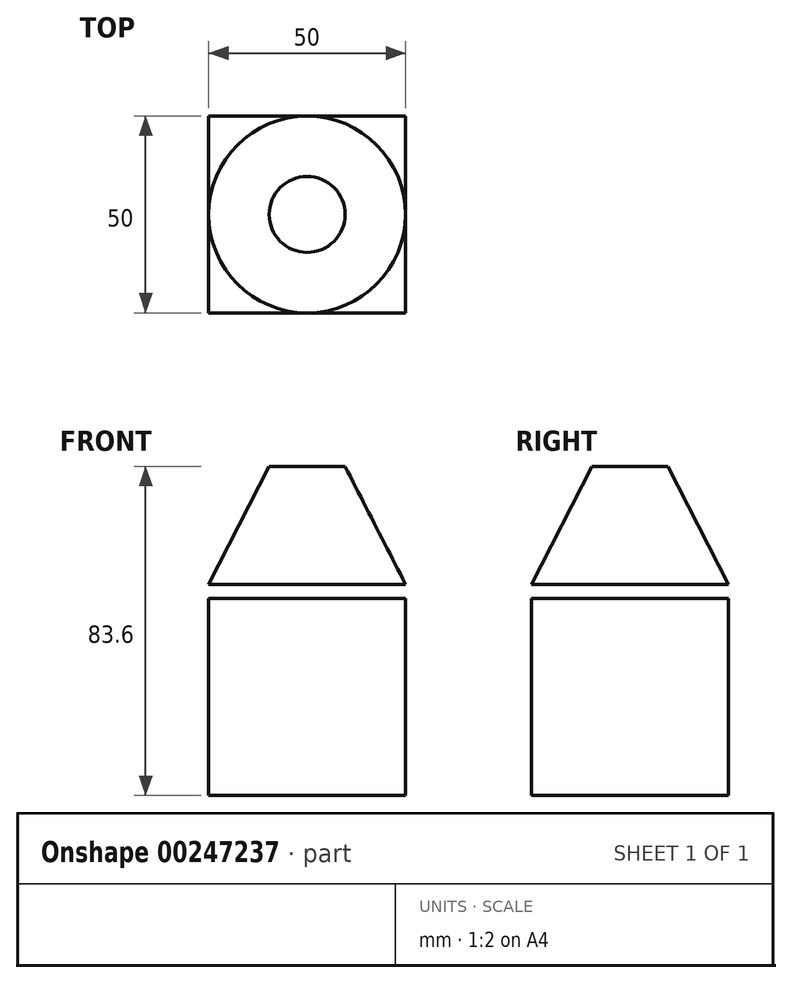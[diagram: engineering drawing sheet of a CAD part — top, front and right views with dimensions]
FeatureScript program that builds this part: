
annotation { "Feature Type Name" : "Feature", "Feature Type Description" : "" }
export const myFeature = defineFeature(function(context is Context, id is Id, definition is map)
    precondition{}
    {
        {
            var Q0;
            Q0=qCreatedBy(makeId("Top.planeOp"),FACE);
            var sketch = newSketch(context, id + "F0", { "sketchPlane" : qUnion([Q0])});
            skLineSegment(sketch, "E0.bottom", {"start": v(25, 25) * mm, "end": v(-25, 25) * mm});
            skLineSegment(sketch, "E0.top", {"start": v(25, -25) * mm, "end": v(-25, -25) * mm});
            skLineSegment(sketch, "E0.left", {"start": v(25, 25) * mm, "end": v(25, -25) * mm});
            skLineSegment(sketch, "E0.right", {"start": v(-25, 25) * mm, "end": v(-25, -25) * mm});
            skPoint(sketch, "E0.middle", {"position": v(0, 0) * mm});
            skSolve(sketch);
        }
        {
            var Q0;
            Q0 = qSketchRegion(id + "F0", true);
            extrude(context, id + "F1", {"entities" : qUnion([Q0]), "endBound" : BoundingType.SYMMETRIC, "depth" : 50 * mm});
        }
        {
            var Q0;
            Q0=qCreatedBy(makeId("Front.planeOp"),FACE);
            var sketch = newSketch(context, id + "F2", { "sketchPlane" : qUnion([Q0])});
            skLineSegment(sketch, "E1", {"start": v(0, 72.89) * mm, "end": v(0, -34.3) * mm, "construction": true});
            skSolve(sketch);
        }
        {
            var Q0;
            Q0=qCreatedBy(makeId("Front.planeOp"),FACE);
            var sketch = newSketch(context, id + "F3", { "sketchPlane" : qUnion([Q0])});
            skLineSegment(sketch, "E2", {"start": v(0, 58.6) * mm, "end": v(-9.65, 58.6) * mm});
            skLineSegment(sketch, "E3", {"start": v(-9.65, 58.6) * mm, "end": v(-25, 28.6) * mm});
            skLineSegment(sketch, "E4", {"start": v(-25, 28.6) * mm, "end": v(0, 28.6) * mm});
            skLineSegment(sketch, "E5", {"start": v(0, 28.6) * mm, "end": v(0, 58.6) * mm});
            skLineSegment(sketch, "E6", {"start": v(-63.94, 24.96) * mm, "end": v(-13.94, 25.65) * mm, "construction": true});
            skSolve(sketch);
        }
        {
            var Q0;
            Q0 = qSketchRegion(id + "F3", true);
            var Q1;
            Q1=sQuery(id+"F2.wireOp",EDGE,"E1");
            revolve(context, id + "F4", {"entities" : qUnion([Q0]), "axis" : qUnion([Q1]), "revolveType" : RevolveType.FULL});
        }
    });
